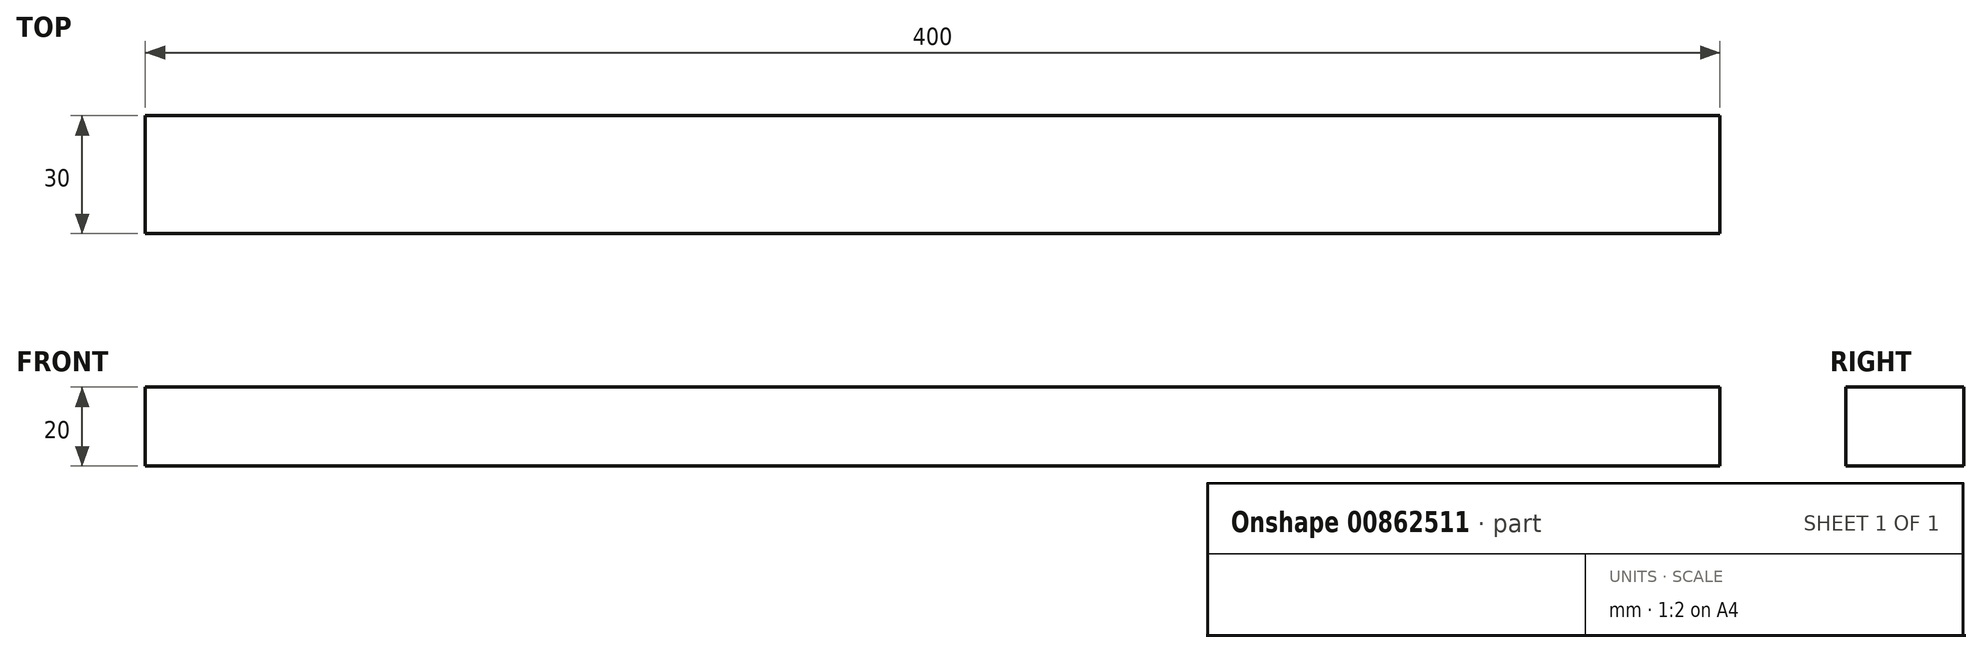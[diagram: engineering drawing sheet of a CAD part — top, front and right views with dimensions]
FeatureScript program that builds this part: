
annotation { "Feature Type Name" : "Feature", "Feature Type Description" : "" }
export const myFeature = defineFeature(function(context is Context, id is Id, definition is map)
    precondition{}
    {
        {
            var Q0;
            Q0=qCreatedBy(makeId("Top.planeOp"),FACE);
            var sketch = newSketch(context, id + "F0", { "sketchPlane" : qUnion([Q0])});
            skLineSegment(sketch, "E0.bottom", {"start": v(0, 0) * mm, "end": v(-400, 0) * mm});
            skLineSegment(sketch, "E0.top", {"start": v(0, -30) * mm, "end": v(-400, -30) * mm});
            skLineSegment(sketch, "E0.left", {"start": v(0, 0) * mm, "end": v(0, -30) * mm});
            skLineSegment(sketch, "E0.right", {"start": v(-400, 0) * mm, "end": v(-400, -30) * mm});
            skSolve(sketch);
        }
        {
            var Q0;
            Q0=makeQuery(id+"F0.imprint","IMPRINT",FACE,{"disambiguationData":[TD([[makeQuery(id+"F0.imprint","IMPRINT",EDGE,{"derivedFrom":sQuery(id+"F0.wireOp",EDGE,"E0.bottom")}),1.0]])]});
            extrude(context, id + "F1", {"entities" : qUnion([Q0]), "depth" : 20 * mm, "offsetDistance" : 25 * mm});
        }
    });
